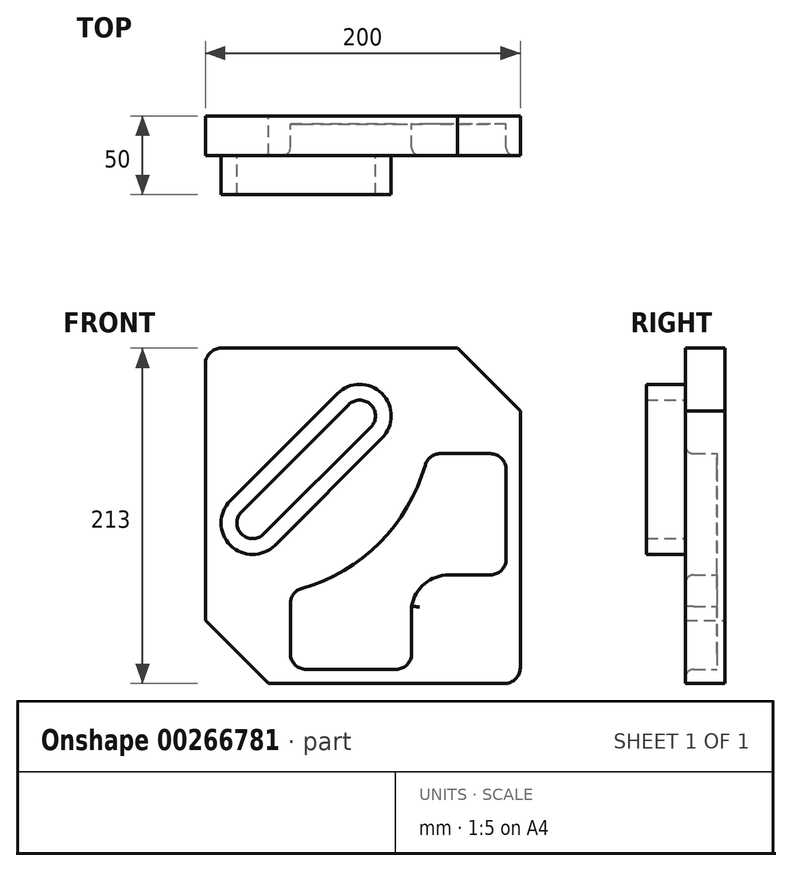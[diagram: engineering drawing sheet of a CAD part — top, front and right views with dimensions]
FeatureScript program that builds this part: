
annotation { "Feature Type Name" : "Feature", "Feature Type Description" : "" }
export const myFeature = defineFeature(function(context is Context, id is Id, definition is map)
    precondition{}
    {
        {
            var Q0;
            Q0=qCreatedBy(makeId("Front.planeOp"),FACE);
            var sketch = newSketch(context, id + "F0", { "sketchPlane" : qUnion([Q0])});
            skLineSegment(sketch, "E0.bottom", {"start": v(100, 106.5) * mm, "end": v(-90, 106.5) * mm});
            skLineSegment(sketch, "E0.top", {"start": v(90, -106.5) * mm, "end": v(-100, -106.5) * mm});
            skLineSegment(sketch, "E0.left", {"start": v(100, 106.5) * mm, "end": v(100, -96.5) * mm});
            skLineSegment(sketch, "E0.right", {"start": v(-100, 96.5) * mm, "end": v(-100, -106.5) * mm});
            skPoint(sketch, "E0.middle", {"position": v(0, 0) * mm});
            skPoint(sketch, "E1.visualSharp", {"position": v(-100, 106.5) * mm});
            skArc(sketch, "E1.filletArc", {"start": v(-90, 106.5) * mm, "mid": v(-97.07, 103.57) * mm, "end": v(-100, 96.5) * mm});
            skPoint(sketch, "E2.visualSharp", {"position": v(100, -106.5) * mm});
            skArc(sketch, "E2.filletArc", {"start": v(90, -106.5) * mm, "mid": v(97.07, -103.57) * mm, "end": v(100, -96.5) * mm});
            skCircle(sketch, "E3", {"center": v(-2, 63.5) * mm, "radius": 10 * mm});
            skCircle(sketch, "E4", {"center": v(-70, -4.5) * mm, "radius": 10 * mm});
            skLineSegment(sketch, "E5", {"start": v(-70, -4.5) * mm, "end": v(-2, 63.5) * mm, "construction": true});
            skArc(sketch, "E6.0.startCap", {"start": v(-62.93, -11.57) * mm, "mid": v(-77.07, -11.57) * mm, "end": v(-77.07, 2.57) * mm});
            skArc(sketch, "E6.0.endCap", {"start": v(-9.07, 70.57) * mm, "mid": v(5.07, 70.57) * mm, "end": v(5.07, 56.43) * mm});
            skLineSegment(sketch, "E6.0.left", {"start": v(-77.07, 2.57) * mm, "end": v(-9.07, 70.57) * mm});
            skLineSegment(sketch, "E6.0.right", {"start": v(-62.93, -11.57) * mm, "end": v(5.07, 56.43) * mm});
            skArc(sketch, "E7.0.startCap", {"start": v(-55.86, -18.64) * mm, "mid": v(-84.14, -18.64) * mm, "end": v(-84.14, 9.64) * mm});
            skArc(sketch, "E7.0.endCap", {"start": v(-16.14, 77.64) * mm, "mid": v(12.14, 77.64) * mm, "end": v(12.14, 49.36) * mm});
            skLineSegment(sketch, "E7.0.left", {"start": v(-84.14, 9.64) * mm, "end": v(-16.14, 77.64) * mm});
            skLineSegment(sketch, "E7.0.right", {"start": v(-55.86, -18.64) * mm, "end": v(12.14, 49.36) * mm});
            skArc(sketch, "E8", {"start": v(-38.74, -46.13) * mm, "mid": v(10.61, -17.11) * mm, "end": v(39.63, 32.24) * mm});
            skLineSegment(sketch, "E9", {"start": v(-2, 63.5) * mm, "end": v(-70, 63.5) * mm, "construction": true});
            skLineSegment(sketch, "E10", {"start": v(-70, -4.5) * mm, "end": v(-70, 63.5) * mm, "construction": true});
            skLineSegment(sketch, "E11", {"start": v(49.25, 39.5) * mm, "end": v(81, 39.5) * mm});
            skLineSegment(sketch, "E12", {"start": v(91, 29.5) * mm, "end": v(91, -27.5) * mm});
            skLineSegment(sketch, "E13", {"start": v(31, -57.43) * mm, "end": v(31, -87.5) * mm});
            skLineSegment(sketch, "E14", {"start": v(21, -97.5) * mm, "end": v(-36, -97.5) * mm});
            skLineSegment(sketch, "E15", {"start": v(-46, -87.5) * mm, "end": v(-46, -55.75) * mm});
            skPoint(sketch, "E16.visualSharp", {"position": v(41.45, 39.5) * mm});
            skArc(sketch, "E16.filletArc", {"start": v(49.25, 39.5) * mm, "mid": v(43.22, 37.48) * mm, "end": v(39.63, 32.24) * mm});
            skPoint(sketch, "E17.visualSharp", {"position": v(91, 39.5) * mm});
            skArc(sketch, "E17.filletArc", {"start": v(91, 29.5) * mm, "mid": v(88.07, 36.57) * mm, "end": v(81, 39.5) * mm});
            skPoint(sketch, "E18.visualSharp", {"position": v(31, -97.5) * mm});
            skArc(sketch, "E18.filletArc", {"start": v(21, -97.5) * mm, "mid": v(28.07, -94.57) * mm, "end": v(31, -87.5) * mm});
            skPoint(sketch, "E19.visualSharp", {"position": v(-46, -97.5) * mm});
            skArc(sketch, "E19.filletArc", {"start": v(-46, -87.5) * mm, "mid": v(-43.07, -94.57) * mm, "end": v(-36, -97.5) * mm});
            skPoint(sketch, "E20.visualSharp", {"position": v(-46, -47.95) * mm});
            skArc(sketch, "E20.filletArc", {"start": v(-38.74, -46.13) * mm, "mid": v(-43.98, -49.72) * mm, "end": v(-46, -55.75) * mm});
            skPoint(sketch, "E21.visualSharp", {"position": v(91, 0) * mm});
            skLineSegment(sketch, "E22", {"start": v(81, -37.5) * mm, "end": v(54.65, -37.5) * mm});
            skArc(sketch, "E23", {"start": v(54.65, -37.5) * mm, "mid": v(39.19, -43.15) * mm, "end": v(31, -57.43) * mm});
            skPoint(sketch, "E24.visualSharp", {"position": v(91, -37.5) * mm});
            skArc(sketch, "E24.filletArc", {"start": v(81, -37.5) * mm, "mid": v(88.07, -34.57) * mm, "end": v(91, -27.5) * mm});
            skLineSegment(sketch, "E25", {"start": v(60, 106.5) * mm, "end": v(100, 66.5) * mm});
            skLineSegment(sketch, "E26", {"start": v(-100, -66.5) * mm, "end": v(-60, -106.5) * mm});
            skSolve(sketch);
        }
        {
            var Q0;
            {var subQ0=sQuery(id+"F0.wireOp",EDGE,"E1.filletArc");Q0=makeQuery(id+"F0.imprint","IMPRINT",FACE,{"disambiguationData":[TD([[makeQuery(id+"F0.imprint","IMPRINT",EDGE,{"derivedFrom":subQ0}),1.0]])]});}
            extrude(context, id + "F1", {"entities" : qUnion([Q0]), "depth" : 25 * mm});
        }
        {
            var Q0;
            {var subQ1=sQuery(id+"F0.wireOp",EDGE,"E6.0.left");Q0=makeQuery(id+"F0.imprint","IMPRINT",FACE,{"disambiguationData":[TD([[makeQuery(id+"F0.imprint","IMPRINT",EDGE,{"derivedFrom":subQ1}),1.0]])]});}
            extrude(context, id + "F2", {"entities" : qUnion([Q0]), "operationType" : NewBodyOperationType.ADD, "depth" : 50 * mm});
        }
        {
            var Q0;
            Q0=makeQuery(id+"F0.imprint","IMPRINT",FACE,{"disambiguationData":[TD([[makeQuery(id+"F0.imprint","IMPRINT",EDGE,{"derivedFrom":sQuery(id+"F0.wireOp",EDGE,"E8")}),-1.0]])]});
            extrude(context, id + "F3", {"entities" : qUnion([Q0]), "operationType" : NewBodyOperationType.ADD, "depth" : 5 * mm});
        }
        {
            var Q0;
            {var subQ0=sQuery(id+"F0.wireOp",EDGE,"E6.0.left");Q0=makeQuery(id+"F0.imprint","IMPRINT",FACE,{"disambiguationData":[TD([[makeQuery(id+"F0.imprint","IMPRINT",EDGE,{"derivedFrom":subQ0}),-1.0]])]});}
            var Q1;
            {var subQ0=sQuery(id+"F0.wireOp",EDGE,"E4");var subQ1=makeQuery(id+"F0.imprint","INTERSECT",VERTEX,{"derivedFrom":[subQ0,sQuery(id+"F0.wireOp",EDGE,"E6.0.left")]});Q1=makeQuery(id+"F0.imprint","IMPRINT",FACE,{"disambiguationData":[TD([[makeQuery(id+"F0.imprint","IMPRINT",EDGE,{"disambiguationData":[TD([[subQ1,-1.0]])],"derivedFrom":subQ0}),1.0]])]});}
            var Q2;
            {var subQ0=sQuery(id+"F0.wireOp",EDGE,"E3");var subQ1=makeQuery(id+"F0.imprint","INTERSECT",VERTEX,{"derivedFrom":[subQ0,sQuery(id+"F0.wireOp",EDGE,"E6.0.left")]});Q2=makeQuery(id+"F0.imprint","IMPRINT",FACE,{"disambiguationData":[TD([[makeQuery(id+"F0.imprint","IMPRINT",EDGE,{"disambiguationData":[TD([[subQ1,-1.0]])],"derivedFrom":subQ0}),1.0]])]});}
            extrude(context, id + "F4", {"entities" : qUnion([Q0, Q1, Q2]), "operationType" : NewBodyOperationType.ADD, "depth" : 25 * mm});
        }
        {
            var Q0;
            Q0=makeQuery(id+"F1.opExtrude","CAP_EDGE",EDGE,{"disambiguationData":[OSD([sQuery(id+"F0.wireOp",EDGE,"E7.0.endCap")])],"isStart":false});
            var Q1;
            Q1=makeQuery(id+"F3.opExtrude","CAP_EDGE",EDGE,{"disambiguationData":[OSD([sQuery(id+"F0.wireOp",EDGE,"E11")])],"isStart":false});
            var Q2;
            Q2=makeQuery(id+"F1.opExtrude","CAP_EDGE",EDGE,{"disambiguationData":[OSD([sQuery(id+"F0.wireOp",EDGE,"E8")])],"isStart":false});
            fillet(context, id + "F5", {"entities" : qUnion([Q0, Q1, Q2]), "radius" : 5 * mm, "tangentPropagation" : true, "allowEdgeOverflow" : false});
        }
    });
